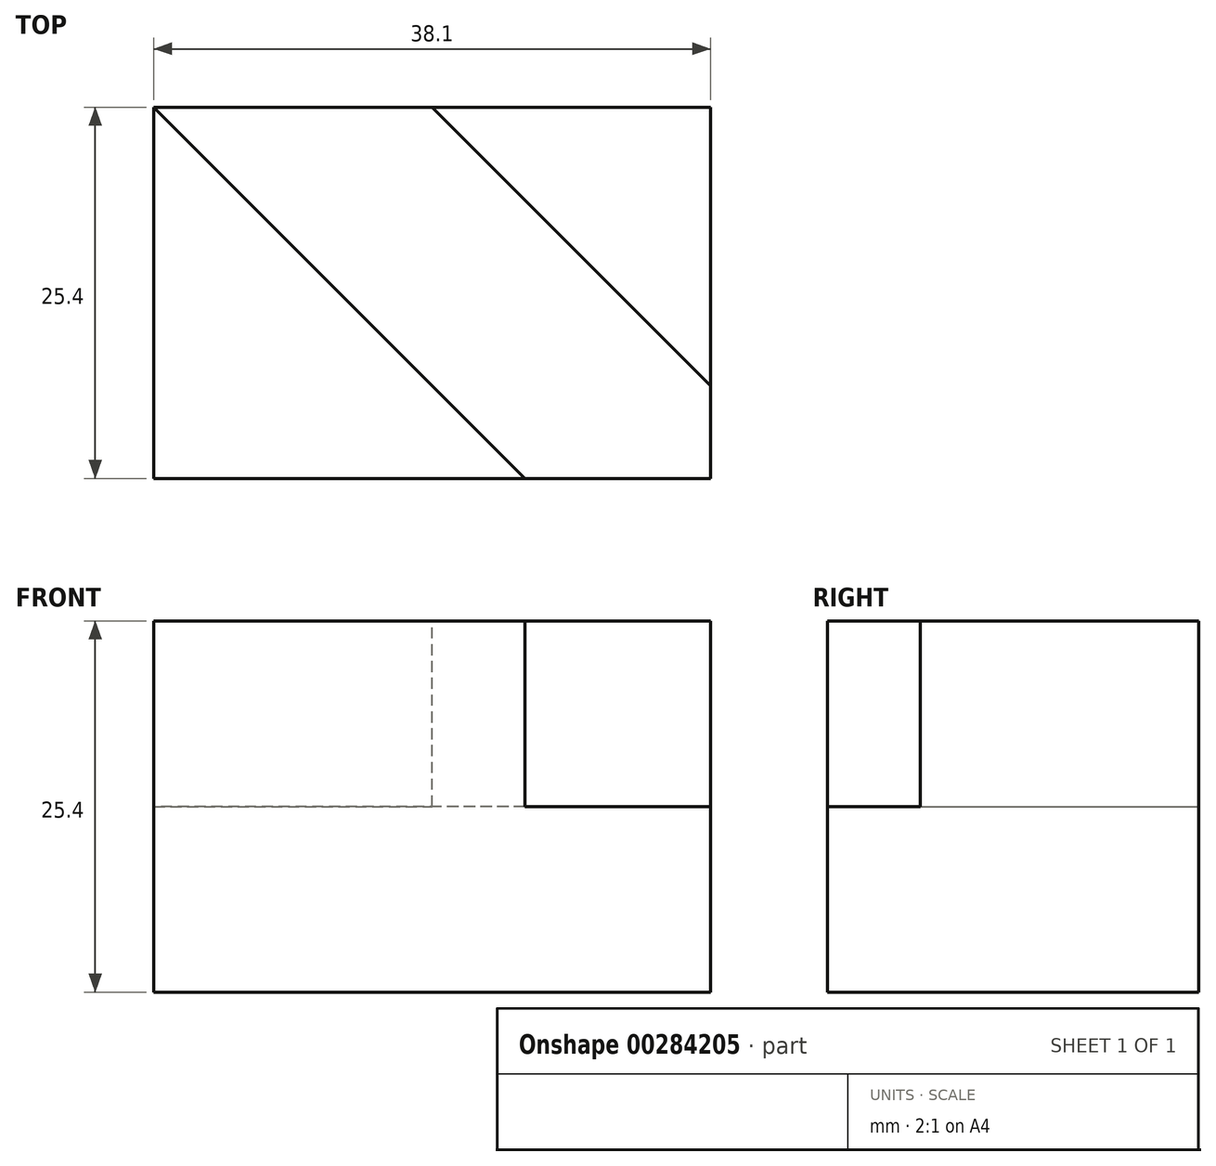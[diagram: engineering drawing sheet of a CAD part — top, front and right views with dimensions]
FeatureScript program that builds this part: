
annotation { "Feature Type Name" : "Feature", "Feature Type Description" : "" }
export const myFeature = defineFeature(function(context is Context, id is Id, definition is map)
    precondition{}
    {
        {
            var Q0;
            Q0=qCreatedBy(makeId("Front.planeOp"),FACE);
            var sketch = newSketch(context, id + "F0", { "sketchPlane" : qUnion([Q0])});
            skLineSegment(sketch, "E0.bottom", {"start": v(0, 0) * mm, "end": v(38.1, 0) * mm});
            skLineSegment(sketch, "E0.top", {"start": v(0, 25.4) * mm, "end": v(38.1, 25.4) * mm});
            skLineSegment(sketch, "E0.left", {"start": v(0, 0) * mm, "end": v(0, 25.4) * mm});
            skLineSegment(sketch, "E0.right", {"start": v(38.1, 0) * mm, "end": v(38.1, 25.4) * mm});
            skSolve(sketch);
        }
        {
            var Q0;
            Q0 = qSketchRegion(id + "F0", true);
            extrude(context, id + "F1", {"entities" : qUnion([Q0]), "depth" : 25.4 * mm});
        }
        {
            var Q0;
            Q0=makeQuery(id+"F1.opExtrude","SWEPT_FACE",FACE,{"disambiguationData":[OSD([sQuery(id+"F0.wireOp",EDGE,"E0.top")])]});
            var sketch = newSketch(context, id + "F2", { "sketchPlane" : qUnion([Q0])});
            skLineSegment(sketch, "E1", {"start": v(38.1, -25.4) * mm, "end": v(25.4, -25.4) * mm});
            skLineSegment(sketch, "E2", {"start": v(25.4, -25.4) * mm, "end": v(0, 0) * mm});
            skLineSegment(sketch, "E3", {"start": v(0, 0) * mm, "end": v(19.05, 0) * mm});
            skLineSegment(sketch, "E4", {"start": v(38.1, -25.4) * mm, "end": v(38.1, -19.05) * mm});
            skLineSegment(sketch, "E5", {"start": v(38.1, -19.05) * mm, "end": v(19.05, 0) * mm});
            skSolve(sketch);
        }
        {
            var Q0;
            Q0=makeQuery(id+"F2.imprint","IMPRINT",FACE,{"disambiguationData":[TD([[makeQuery(id+"F2.imprint","IMPRINT",EDGE,{"derivedFrom":sQuery(id+"F2.wireOp",EDGE,"E1")}),1.0]])]});
            extrude(context, id + "F3", {"entities" : qUnion([Q0]), "operationType" : NewBodyOperationType.REMOVE, "oppositeDirection" : true, "depth" : 12.7 * mm});
        }
    });
